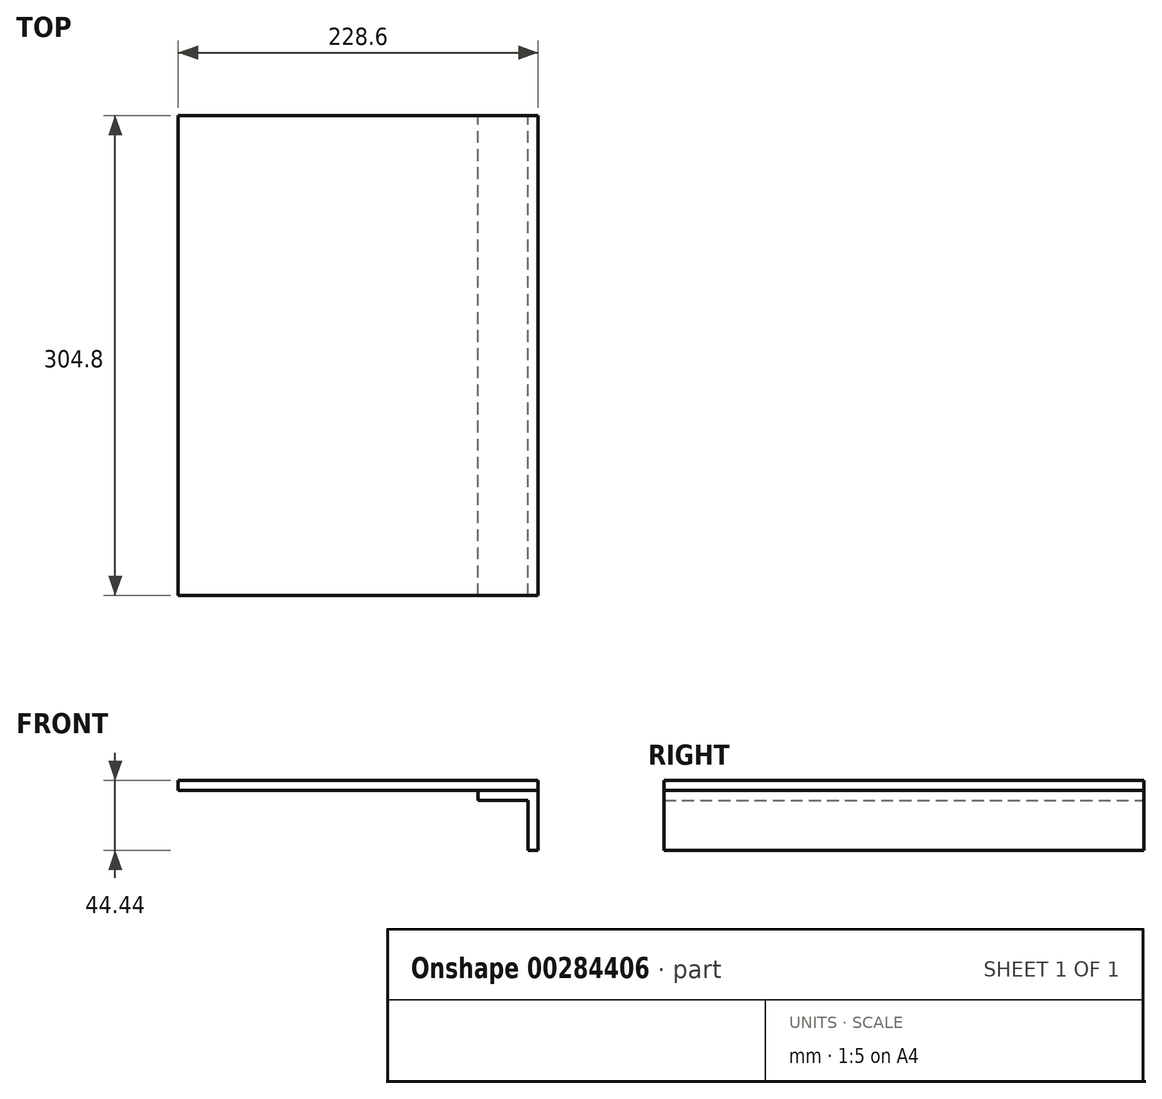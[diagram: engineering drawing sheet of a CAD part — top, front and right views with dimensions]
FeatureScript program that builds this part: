
annotation { "Feature Type Name" : "Feature", "Feature Type Description" : "" }
export const myFeature = defineFeature(function(context is Context, id is Id, definition is map)
    precondition{}
    {
        {
            var Q0;
            Q0=qCreatedBy(makeId("Front.planeOp"),FACE);
            var sketch = newSketch(context, id + "F0", { "sketchPlane" : qUnion([Q0])});
            skLineSegment(sketch, "E0.bottom", {"start": v(114.3, -3.17) * mm, "end": v(-114.3, -3.18) * mm});
            skLineSegment(sketch, "E0.top", {"start": v(114.3, 3.18) * mm, "end": v(-114.3, 3.17) * mm});
            skLineSegment(sketch, "E0.left", {"start": v(114.3, -3.17) * mm, "end": v(114.3, 3.18) * mm});
            skLineSegment(sketch, "E0.right", {"start": v(-114.3, -3.18) * mm, "end": v(-114.3, 3.17) * mm});
            skPoint(sketch, "E0.middle", {"position": v(0, 0) * mm});
            skLineSegment(sketch, "E1", {"start": v(76.2, -3.17) * mm, "end": v(76.2, -9.52) * mm});
            skLineSegment(sketch, "E2", {"start": v(76.2, -9.52) * mm, "end": v(107.95, -9.52) * mm});
            skLineSegment(sketch, "E3", {"start": v(107.95, -9.52) * mm, "end": v(107.95, -41.27) * mm});
            skLineSegment(sketch, "E4", {"start": v(107.95, -41.27) * mm, "end": v(114.3, -41.27) * mm});
            skLineSegment(sketch, "E5", {"start": v(114.3, -41.27) * mm, "end": v(114.3, -3.17) * mm});
            skSolve(sketch);
        }
        {
            var Q0;
            Q0=makeQuery(id+"F0.imprint","IMPRINT",FACE,{"disambiguationData":[TD([[makeQuery(id+"F0.imprint","IMPRINT",EDGE,{"derivedFrom":sQuery(id+"F0.wireOp",EDGE,"E0.bottom")}),-1.0]])]});
            extrude(context, id + "F1", {"entities" : qUnion([Q0]), "endBound" : BoundingType.SYMMETRIC, "depth" : 304.8 * mm});
        }
        {
            var Q0;
            {var subQ0=sQuery(id+"F0.wireOp",EDGE,"E1");Q0=makeQuery(id+"F0.imprint","IMPRINT",FACE,{"disambiguationData":[TD([[makeQuery(id+"F0.imprint","IMPRINT",EDGE,{"derivedFrom":subQ0}),1.0]])]});}
            extrude(context, id + "F2", {"entities" : qUnion([Q0]), "endBound" : BoundingType.SYMMETRIC, "depth" : 304.8 * mm});
        }
    });
